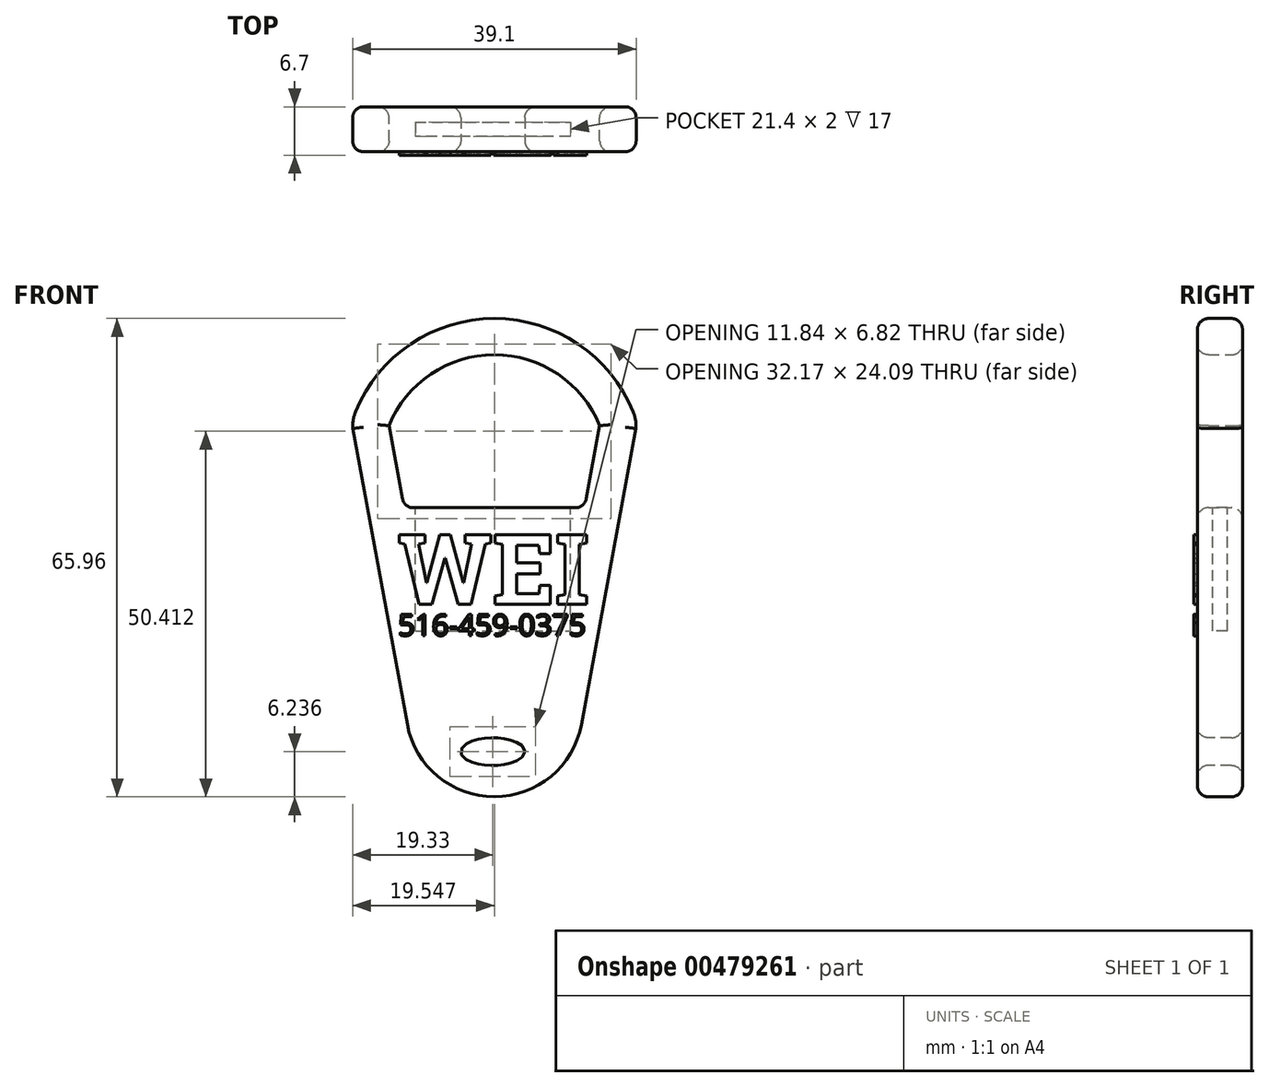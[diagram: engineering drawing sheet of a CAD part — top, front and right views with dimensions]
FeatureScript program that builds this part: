
annotation { "Feature Type Name" : "Feature", "Feature Type Description" : "" }
export const myFeature = defineFeature(function(context is Context, id is Id, definition is map)
    precondition{}
    {
        {
            var Q0;
            Q0=qCreatedBy(makeId("Front.planeOp"),FACE);
            var sketch = newSketch(context, id + "F0", { "sketchPlane" : qUnion([Q0])});
            skLineSegment(sketch, "E0", {"start": v(0.22, 53.5) * mm, "end": v(0.22, -27.22) * mm, "construction": true});
            skLineSegment(sketch, "E1", {"start": v(19.76, 12.33) * mm, "end": v(12.22, -28.48) * mm});
            skLineSegment(sketch, "E2.MirrorCS", {"start": v(-19.33, 12.33) * mm, "end": v(-11.78, -28.48) * mm});
            skLineSegment(sketch, "E3.0", {"start": v(-14.31, 12.71) * mm, "end": v(-12.22, 1.4) * mm});
            skLineSegment(sketch, "E3.3", {"start": v(14.75, 12.71) * mm, "end": v(12.66, 1.4) * mm});
            skLineSegment(sketch, "E4", {"start": v(-12.22, 1.4) * mm, "end": v(12.66, 1.4) * mm});
            skPoint(sketch, "E5", {"position": v(0.22, 20.6) * mm});
            skPoint(sketch, "E6", {"position": v(-14.31, 12.71) * mm});
            skPoint(sketch, "E7.MirrorP", {"position": v(14.75, 12.71) * mm});
            skArc(sketch, "E8", {"start": v(14.75, 12.71) * mm, "mid": v(0.22, 22.5) * mm, "end": v(-14.31, 12.71) * mm});
            skArc(sketch, "E9.0", {"start": v(19.62, 13.97) * mm, "mid": v(0.56, 27.5) * mm, "end": v(-18.94, 14.6) * mm});
            skArc(sketch, "E10", {"start": v(-18.94, 14.6) * mm, "mid": v(-19.26, 13.5) * mm, "end": v(-19.33, 12.33) * mm});
            skArc(sketch, "E11.MirrorCS", {"start": v(19.38, 14.6) * mm, "mid": v(19.7, 13.5) * mm, "end": v(19.76, 12.33) * mm});
            skPoint(sketch, "E12.orphan", {"position": v(-21.9, 26.19) * mm});
            skPoint(sketch, "E13.orphan", {"position": v(22.32, 26.19) * mm});
            skPoint(sketch, "E14.MirrorCS.start.orphan", {"position": v(0.22, 25.6) * mm});
            skArc(sketch, "E15", {"start": v(-11.78, -28.48) * mm, "mid": v(0.22, -38.46) * mm, "end": v(12.22, -28.48) * mm});
            skPoint(sketch, "E16.MirrorCS.end.orphan", {"position": v(0.22, -28.48) * mm});
            skPoint(sketch, "E16.MirrorCS.start.orphan", {"position": v(-11.78, -28.48) * mm});
            skLineSegment(sketch, "E17", {"start": v(-11.78, -28.48) * mm, "end": v(12.22, -28.48) * mm, "construction": true});
            skSolve(sketch);
        }
        {
            var Q0;
            Q0=qSketchRegion(id+"F0",true);
            extrude(context, id + "F1", {"entities" : qUnion([Q0]), "depth" : 6.2 * mm});
        }
        {
            var Q0;
            Q0=makeQuery(id+"F1.opExtrude","CAP_FACE",FACE,{"disambiguationData":[OSD([sQuery(id+"F0.wireOp",EDGE,"E1"),sQuery(id+"F0.wireOp",EDGE,"E2.MirrorCS"),sQuery(id+"F0.wireOp",EDGE,"E3.0"),sQuery(id+"F0.wireOp",EDGE,"E3.3"),sQuery(id+"F0.wireOp",EDGE,"E4"),sQuery(id+"F0.wireOp",EDGE,"E8"),sQuery(id+"F0.wireOp",EDGE,"E9.0"),sQuery(id+"F0.wireOp",EDGE,"E10"),sQuery(id+"F0.wireOp",EDGE,"E11.MirrorCS"),sQuery(id+"F0.wireOp",EDGE,"E15")])],"isStart":false});
            var sketch = newSketch(context, id + "F2", { "sketchPlane" : qUnion([Q0])});
            skEllipse(sketch, "E18", {"center": v(0, -32.22) * mm, "majorRadius": 4.42 * mm, "minorRadius": 1.9 * mm, "majorAxis": v(1, 0)});
            skSolve(sketch);
        }
        {
            var Q0;
            Q0=makeQuery(id+"F2.imprint","IMPRINT",FACE,{"disambiguationData":[TD([[makeQuery(id+"F2.imprint","IMPRINT",EDGE,{"derivedFrom":sQuery(id+"F2.wireOp",EDGE,"E18")}),1.0]])]});
            extrude(context, id + "F3", {"entities" : qUnion([Q0]), "operationType" : NewBodyOperationType.REMOVE, "oppositeDirection" : true, "depth" : 6.5 * mm});
        }
        {
            var Q0;
            Q0=makeQuery(id+"F1.opExtrude","SWEPT_FACE",FACE,{"disambiguationData":[OSD([sQuery(id+"F0.wireOp",EDGE,"E4")])]});
            var sketch = newSketch(context, id + "F4", { "sketchPlane" : qUnion([Q0])});
            skLineSegment(sketch, "E19", {"start": v(0, -2.1) * mm, "end": v(10.7, -2.1) * mm});
            skLineSegment(sketch, "E20.0", {"start": v(0, -4.1) * mm, "end": v(10.7, -4.1) * mm});
            skLineSegment(sketch, "E21", {"start": v(10.7, -2.1) * mm, "end": v(10.7, -4.1) * mm});
            skLineSegment(sketch, "E22", {"start": v(0, -2.1) * mm, "end": v(0, -4.1) * mm, "construction": true});
            skLineSegment(sketch, "E23.MirrorCS", {"start": v(0, -2.1) * mm, "end": v(-10.7, -2.1) * mm});
            skLineSegment(sketch, "E24.MirrorCS", {"start": v(-10.7, -2.1) * mm, "end": v(-10.7, -4.1) * mm});
            skLineSegment(sketch, "E25.MirrorCS", {"start": v(0, -4.1) * mm, "end": v(-10.7, -4.1) * mm});
            skSolve(sketch);
        }
        {
            var Q0;
            Q0=makeQuery(id+"F4.imprint","IMPRINT",FACE,{"disambiguationData":[TD([[makeQuery(id+"F4.imprint","IMPRINT",EDGE,{"derivedFrom":sQuery(id+"F4.wireOp",EDGE,"E19")}),-1.0]])]});
            extrude(context, id + "F5", {"entities" : qUnion([Q0]), "operationType" : NewBodyOperationType.REMOVE, "oppositeDirection" : true, "offsetDistance" : 25 * mm, "depth" : 17 * mm});
        }
        {
            var Q0;
            Q0=makeQuery(id+"F1.opExtrude","SWEPT_EDGE",EDGE,{"disambiguationData":[OSD([sQuery(id+"F0.wireOp",EDGE,"E3.0"),sQuery(id+"F0.wireOp",EDGE,"E4")])]});
            var Q1;
            Q1=makeQuery(id+"F1.opExtrude","SWEPT_EDGE",EDGE,{"disambiguationData":[OSD([sQuery(id+"F0.wireOp",EDGE,"E3.3"),sQuery(id+"F0.wireOp",EDGE,"E4")])]});
            var Q2;
            Q2=makeQuery(id+"F1.opExtrude","CAP_FACE",FACE,{"disambiguationData":[OSD([sQuery(id+"F0.wireOp",EDGE,"E1"),sQuery(id+"F0.wireOp",EDGE,"E2.MirrorCS"),sQuery(id+"F0.wireOp",EDGE,"E3.0"),sQuery(id+"F0.wireOp",EDGE,"E3.3"),sQuery(id+"F0.wireOp",EDGE,"E4"),sQuery(id+"F0.wireOp",EDGE,"E8"),sQuery(id+"F0.wireOp",EDGE,"E9.0"),sQuery(id+"F0.wireOp",EDGE,"E10"),sQuery(id+"F0.wireOp",EDGE,"E11.MirrorCS"),sQuery(id+"F0.wireOp",EDGE,"E15")])],"isStart":false});
            var Q3;
            Q3=makeQuery(id+"F1.opExtrude","CAP_FACE",FACE,{"disambiguationData":[OSD([sQuery(id+"F0.wireOp",EDGE,"E1"),sQuery(id+"F0.wireOp",EDGE,"E2.MirrorCS"),sQuery(id+"F0.wireOp",EDGE,"E3.0"),sQuery(id+"F0.wireOp",EDGE,"E3.3"),sQuery(id+"F0.wireOp",EDGE,"E4"),sQuery(id+"F0.wireOp",EDGE,"E8"),sQuery(id+"F0.wireOp",EDGE,"E9.0"),sQuery(id+"F0.wireOp",EDGE,"E10"),sQuery(id+"F0.wireOp",EDGE,"E11.MirrorCS"),sQuery(id+"F0.wireOp",EDGE,"E15")])],"isStart":true});
            fillet(context, id + "F6", {"entities" : qUnion([Q0, Q1, Q2, Q3]), "radius" : 1.5 * mm, "tangentPropagation" : true, "allowEdgeOverflow" : false});
        }
        {
            var Q0;
            Q0=makeQuery(id+"F1.opExtrude","CAP_FACE",FACE,{"disambiguationData":[OSD([sQuery(id+"F0.wireOp",EDGE,"E1"),sQuery(id+"F0.wireOp",EDGE,"E2.MirrorCS"),sQuery(id+"F0.wireOp",EDGE,"E3.0"),sQuery(id+"F0.wireOp",EDGE,"E3.3"),sQuery(id+"F0.wireOp",EDGE,"E4"),sQuery(id+"F0.wireOp",EDGE,"E8"),sQuery(id+"F0.wireOp",EDGE,"E9.0"),sQuery(id+"F0.wireOp",EDGE,"E10"),sQuery(id+"F0.wireOp",EDGE,"E11.MirrorCS"),sQuery(id+"F0.wireOp",EDGE,"E15")])],"isStart":false});
            var sketch = newSketch(context, id + "F7", { "sketchPlane" : qUnion([Q0])});
            skText(sketch, "E26", { "text": "WEI", "fontName": "RobotoSlab-Bold.ttf"});
            const initialGuessF7  = {"E26": [-0.0131, -0.01193, 1, 0, 0.00975]};
            skSetInitialGuess(sketch, initialGuessF7);
            skSolve(sketch);
        }
        {
            var Q0;
            Q0 = qSketchRegion(id + "F7", true);
            extrude(context, id + "F8", {"entities" : qUnion([Q0]), "operationType" : NewBodyOperationType.ADD, "depth" : .5 * mm, "offsetDistance" : 25 * mm});
        }
        {
            var Q0;
            Q0=makeQuery(id+"F1.opExtrude","CAP_FACE",FACE,{"disambiguationData":[OSD([sQuery(id+"F0.wireOp",EDGE,"E1"),sQuery(id+"F0.wireOp",EDGE,"E2.MirrorCS"),sQuery(id+"F0.wireOp",EDGE,"E3.0"),sQuery(id+"F0.wireOp",EDGE,"E3.3"),sQuery(id+"F0.wireOp",EDGE,"E4"),sQuery(id+"F0.wireOp",EDGE,"E8"),sQuery(id+"F0.wireOp",EDGE,"E9.0"),sQuery(id+"F0.wireOp",EDGE,"E10"),sQuery(id+"F0.wireOp",EDGE,"E11.MirrorCS"),sQuery(id+"F0.wireOp",EDGE,"E15")])],"isStart":false});
            var sketch = newSketch(context, id + "F9", { "sketchPlane" : qUnion([Q0])});
            skText(sketch, "E27", { "text": "516-459-0375", "fontName": "OpenSans-Regular.ttf"});
            const initialGuessF9  = {"E27": [-0.01306, -0.01623, 1, 0, 0.00293]};
            skSetInitialGuess(sketch, initialGuessF9);
            skSolve(sketch);
        }
        {
            var Q0;
            Q0 = qSketchRegion(id + "F9", true);
            extrude(context, id + "F10", {"entities" : qUnion([Q0]), "operationType" : NewBodyOperationType.ADD, "depth" : .5 * mm, "offsetDistance" : 25 * mm});
        }
    });
